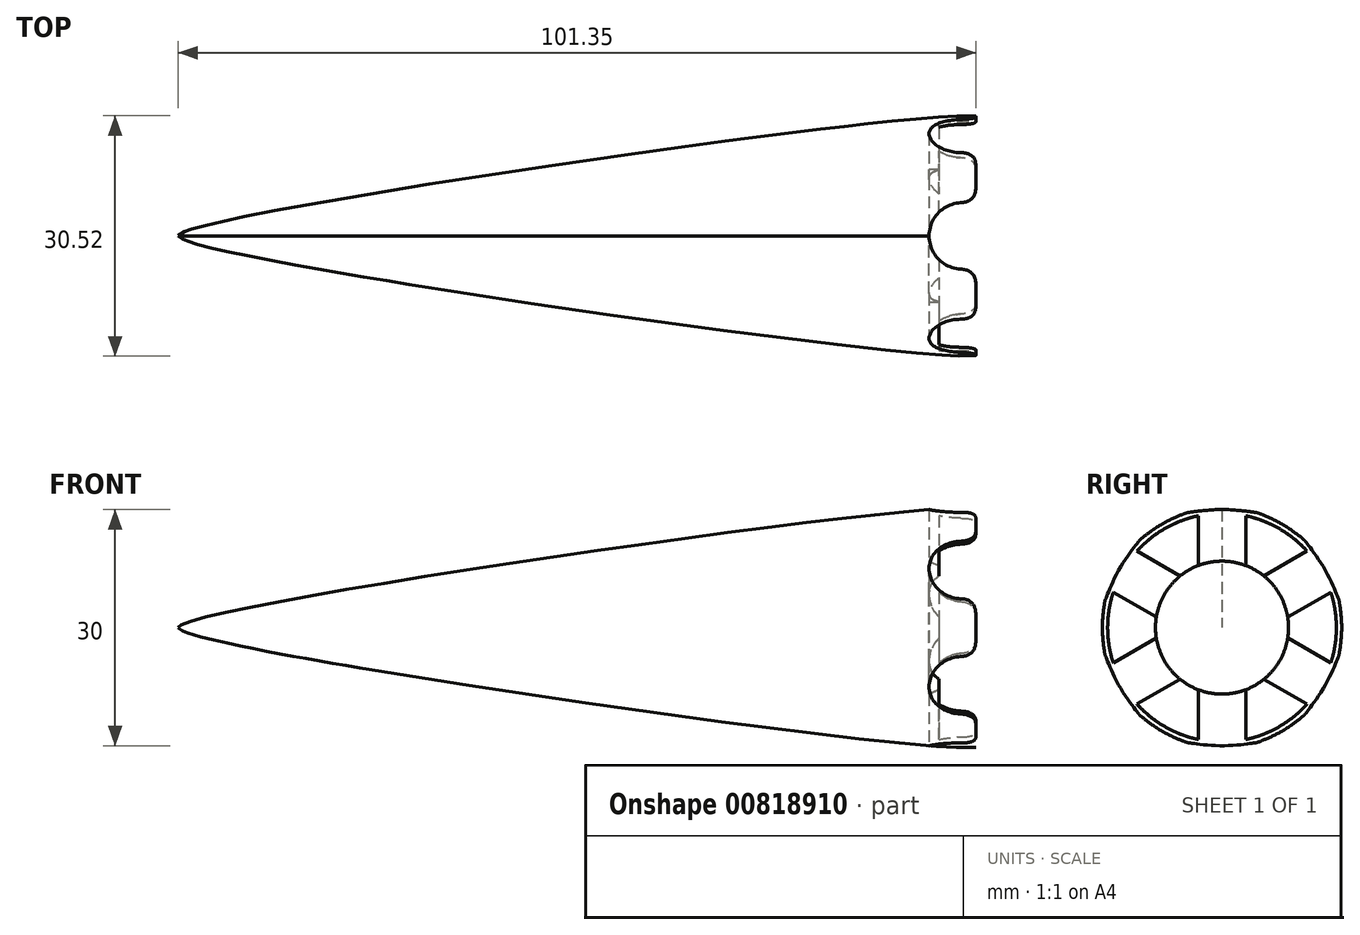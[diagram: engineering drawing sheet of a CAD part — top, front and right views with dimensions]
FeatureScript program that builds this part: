
annotation { "Feature Type Name" : "Feature", "Feature Type Description" : "" }
export const myFeature = defineFeature(function(context is Context, id is Id, definition is map)
    precondition{}
    {
        {
            var Q0;
            Q0=qCreatedBy(makeId("Front.planeOp"),FACE);
            var sketch = newSketch(context, id + "F0", { "sketchPlane" : qUnion([Q0])});
            skFitSpline(sketch, "E0", {"points": [v(1.73, 15.2) * mm, v(-99.62, 0) * mm], "startDerivative": vector(-22.55, 3.1) * mm, "endDerivative": vector(-0.3, -8.2) * mm});
            skLineSegment(sketch, "E1", {"start": v(1.73, 15.2) * mm, "end": v(1.73, 0) * mm});
            skLineSegment(sketch, "E2", {"start": v(1.73, 0) * mm, "end": v(-99.62, 0) * mm});
            skSolve(sketch);
        }
        {
            var Q0;
            Q0=qSketchRegion(id+"F0",true);
            var Q1;
            Q1=sQuery(id+"F0.wireOp",EDGE,"E2");
            revolve(context, id + "F1", {"surfaceOperationType" : NewSurfaceOperationType.NEW, "entities" : qUnion([Q0]), "axis" : qUnion([Q1]), "revolveType" : RevolveType.FULL});
        }
        {
            var Q0;
            Q0=qCreatedBy(makeId("Right.planeOp"),FACE);
            var sketch = newSketch(context, id + "F2", { "sketchPlane" : qUnion([Q0])});
            skCircle(sketch, "E3", {"center": v(0, 0) * mm, "radius": 14.53 * mm});
            skSolve(sketch);
        }
        {
            var Q0;
            Q0=qSketchRegion(id+"F2",true);
            extrude(context, id + "F3", {"entities" : qUnion([Q0]), "operationType" : NewBodyOperationType.REMOVE, "endBound" : BoundingType.SYMMETRIC, "oppositeDirection" : true, "depth" : 5.9 * mm, "offsetDistance" : 25.4 * mm});
        }
        {
            var Q0;
            Q0=qCreatedBy(makeId("Right.planeOp"),FACE);
            var sketch = newSketch(context, id + "F4", { "sketchPlane" : qUnion([Q0])});
            skLineSegment(sketch, "E4.bottom", {"start": v(0, 18.58) * mm, "end": v(-4.22, 18.58) * mm});
            skLineSegment(sketch, "E4.top", {"start": v(0, -18.58) * mm, "end": v(-4.22, -18.58) * mm});
            skLineSegment(sketch, "E4.left", {"start": v(0, 18.58) * mm, "end": v(0, -18.58) * mm});
            skLineSegment(sketch, "E4.right", {"start": v(-4.22, 18.58) * mm, "end": v(-4.22, -18.58) * mm});
            skPoint(sketch, "E4.middle", {"position": v(-2.11, 0) * mm});
            skSolve(sketch);
        }
        {
            var Q0;
            Q0=qCreatedBy(makeId("Right.planeOp"),FACE);
            var sketch = newSketch(context, id + "F5", { "sketchPlane" : qUnion([Q0])});
            skLineSegment(sketch, "E5.bottom", {"start": v(16.1, 9.3) * mm, "end": v(13.98, 12.95) * mm});
            skLineSegment(sketch, "E5.top", {"start": v(-16.1, -9.3) * mm, "end": v(-18.2, -5.63) * mm});
            skLineSegment(sketch, "E5.left", {"start": v(16.1, 9.3) * mm, "end": v(-16.1, -9.3) * mm});
            skLineSegment(sketch, "E5.right", {"start": v(13.98, 12.95) * mm, "end": v(-18.2, -5.63) * mm});
            skPoint(sketch, "E5.middle", {"position": v(-1.06, 1.83) * mm});
            skSolve(sketch);
        }
        {
            var Q0;
            Q0=qCreatedBy(makeId("Right.planeOp"),FACE);
            var sketch = newSketch(context, id + "F6", { "sketchPlane" : qUnion([Q0])});
            skLineSegment(sketch, "E6.bottom", {"start": v(16.1, -9.3) * mm, "end": v(18.2, -5.63) * mm});
            skLineSegment(sketch, "E6.top", {"start": v(-16.1, 9.3) * mm, "end": v(-13.98, 12.95) * mm});
            skLineSegment(sketch, "E6.left", {"start": v(16.1, -9.3) * mm, "end": v(-16.1, 9.3) * mm});
            skLineSegment(sketch, "E6.right", {"start": v(18.2, -5.63) * mm, "end": v(-13.98, 12.95) * mm});
            skPoint(sketch, "E6.middle", {"position": v(1.06, 1.83) * mm});
            skSolve(sketch);
        }
        {
            var Q0;
            Q0=qSketchRegion(id+"F4",true);
            var Q1;
            Q1=sQuery(id+"F4.wireOp",EDGE,"E4.left");
            revolve(context, id + "F7", {"operationType" : NewBodyOperationType.REMOVE, "surfaceOperationType" : NewSurfaceOperationType.NEW, "entities" : qUnion([Q0]), "axis" : qUnion([Q1]), "revolveType" : RevolveType.FULL, "oppositeDirection" : true});
        }
        {
            var Q0;
            Q0=qSketchRegion(id+"F5",true);
            var Q1;
            Q1=sQuery(id+"F5.wireOp",EDGE,"E5.left");
            revolve(context, id + "F8", {"operationType" : NewBodyOperationType.REMOVE, "surfaceOperationType" : NewSurfaceOperationType.NEW, "entities" : qUnion([Q0]), "axis" : qUnion([Q1]), "revolveType" : RevolveType.FULL, "oppositeDirection" : true});
        }
        {
            var Q0;
            Q0=qSketchRegion(id+"F6",true);
            var Q1;
            Q1=sQuery(id+"F6.wireOp",EDGE,"E6.left");
            revolve(context, id + "F9", {"operationType" : NewBodyOperationType.REMOVE, "surfaceOperationType" : NewSurfaceOperationType.NEW, "entities" : qUnion([Q0]), "axis" : qUnion([Q1]), "revolveType" : RevolveType.FULL, "oppositeDirection" : true});
        }
        {
            var Q0;
            Q0=qCreatedBy(makeId("Right.planeOp"),FACE);
            var sketch = newSketch(context, id + "F10", { "sketchPlane" : qUnion([Q0])});
            skCircle(sketch, "E7", {"center": v(0, 0) * mm, "radius": 8.45 * mm});
            skSolve(sketch);
        }
        {
            var Q0;
            Q0=qSketchRegion(id+"F10",true);
            extrude(context, id + "F11", {"entities" : qUnion([Q0]), "operationType" : NewBodyOperationType.REMOVE, "endBound" : BoundingType.SYMMETRIC, "depth" : 8.45 * mm, "offsetDistance" : 25.4 * mm});
        }
        {
            var Q0;
            Q0=makeQuery(id+"F7.boolean.opBoolean","INTERSECT",EDGE,{"disambiguationData":[OD(2.0)],"derivedFrom":[makeQuery(id+"F1.opRevolve","SWEPT_FACE",FACE,{"disambiguationData":[OSD([sQuery(id+"F0.wireOp",EDGE,"E1")])]}),makeQuery(id+"F7.opRevolve","SWEPT_FACE",FACE,{"disambiguationData":[OSD([sQuery(id+"F4.wireOp",EDGE,"E4.right")])]})]});
            var Q1;
            Q1=makeQuery(id+"F9.boolean.opBoolean","INTERSECT",EDGE,{"disambiguationData":[OD(0.0)],"derivedFrom":[makeQuery(id+"F8.boolean.opBoolean","SPLIT",FACE,{"disambiguationData":[OD(1.0)],"derivedFrom":makeQuery(id+"F7.boolean.opBoolean","SPLIT",FACE,{"disambiguationData":[OD(0.0)],"derivedFrom":makeQuery(id+"F1.opRevolve","SWEPT_FACE",FACE,{"disambiguationData":[OSD([sQuery(id+"F0.wireOp",EDGE,"E1")])]})})}),makeQuery(id+"F9.opRevolve","SWEPT_FACE",FACE,{"disambiguationData":[OSD([sQuery(id+"F6.wireOp",EDGE,"E6.right")])]})]});
            var Q2;
            Q2=makeQuery(id+"F9.boolean.opBoolean","INTERSECT",EDGE,{"disambiguationData":[OD(1.0)],"derivedFrom":[makeQuery(id+"F8.boolean.opBoolean","SPLIT",FACE,{"disambiguationData":[OD(1.0)],"derivedFrom":makeQuery(id+"F7.boolean.opBoolean","SPLIT",FACE,{"disambiguationData":[OD(0.0)],"derivedFrom":makeQuery(id+"F1.opRevolve","SWEPT_FACE",FACE,{"disambiguationData":[OSD([sQuery(id+"F0.wireOp",EDGE,"E1")])]})})}),makeQuery(id+"F9.opRevolve","SWEPT_FACE",FACE,{"disambiguationData":[OSD([sQuery(id+"F6.wireOp",EDGE,"E6.right")])]})]});
            var Q3;
            Q3=makeQuery(id+"F8.boolean.opBoolean","INTERSECT",EDGE,{"disambiguationData":[OD(1.0)],"derivedFrom":[makeQuery(id+"F7.boolean.opBoolean","SPLIT",FACE,{"disambiguationData":[OD(0.0)],"derivedFrom":makeQuery(id+"F1.opRevolve","SWEPT_FACE",FACE,{"disambiguationData":[OSD([sQuery(id+"F0.wireOp",EDGE,"E1")])]})}),makeQuery(id+"F8.opRevolve","SWEPT_FACE",FACE,{"disambiguationData":[OSD([sQuery(id+"F5.wireOp",EDGE,"E5.right")])]})]});
            var Q4;
            Q4=makeQuery(id+"F8.boolean.opBoolean","INTERSECT",EDGE,{"disambiguationData":[OD(0.0)],"derivedFrom":[makeQuery(id+"F7.boolean.opBoolean","SPLIT",FACE,{"disambiguationData":[OD(0.0)],"derivedFrom":makeQuery(id+"F1.opRevolve","SWEPT_FACE",FACE,{"disambiguationData":[OSD([sQuery(id+"F0.wireOp",EDGE,"E1")])]})}),makeQuery(id+"F8.opRevolve","SWEPT_FACE",FACE,{"disambiguationData":[OSD([sQuery(id+"F5.wireOp",EDGE,"E5.right")])]})]});
            var Q5;
            Q5=makeQuery(id+"F7.boolean.opBoolean","INTERSECT",EDGE,{"disambiguationData":[OD(0.0)],"derivedFrom":[makeQuery(id+"F1.opRevolve","SWEPT_FACE",FACE,{"disambiguationData":[OSD([sQuery(id+"F0.wireOp",EDGE,"E1")])]}),makeQuery(id+"F7.opRevolve","SWEPT_FACE",FACE,{"disambiguationData":[OSD([sQuery(id+"F4.wireOp",EDGE,"E4.right")])]})]});
            var Q6;
            Q6=makeQuery(id+"F7.boolean.opBoolean","INTERSECT",EDGE,{"disambiguationData":[OD(1.0)],"derivedFrom":[makeQuery(id+"F1.opRevolve","SWEPT_FACE",FACE,{"disambiguationData":[OSD([sQuery(id+"F0.wireOp",EDGE,"E1")])]}),makeQuery(id+"F7.opRevolve","SWEPT_FACE",FACE,{"disambiguationData":[OSD([sQuery(id+"F4.wireOp",EDGE,"E4.right")])]})]});
            var Q7;
            Q7=makeQuery(id+"F9.boolean.opBoolean","INTERSECT",EDGE,{"disambiguationData":[OD(0.0)],"derivedFrom":[makeQuery(id+"F8.boolean.opBoolean","SPLIT",FACE,{"disambiguationData":[OD(0.0)],"derivedFrom":makeQuery(id+"F7.boolean.opBoolean","SPLIT",FACE,{"disambiguationData":[OD(1.0)],"derivedFrom":makeQuery(id+"F1.opRevolve","SWEPT_FACE",FACE,{"disambiguationData":[OSD([sQuery(id+"F0.wireOp",EDGE,"E1")])]})})}),makeQuery(id+"F9.opRevolve","SWEPT_FACE",FACE,{"disambiguationData":[OSD([sQuery(id+"F6.wireOp",EDGE,"E6.right")])]})]});
            var Q8;
            Q8=makeQuery(id+"F9.boolean.opBoolean","INTERSECT",EDGE,{"disambiguationData":[OD(1.0)],"derivedFrom":[makeQuery(id+"F8.boolean.opBoolean","SPLIT",FACE,{"disambiguationData":[OD(0.0)],"derivedFrom":makeQuery(id+"F7.boolean.opBoolean","SPLIT",FACE,{"disambiguationData":[OD(1.0)],"derivedFrom":makeQuery(id+"F1.opRevolve","SWEPT_FACE",FACE,{"disambiguationData":[OSD([sQuery(id+"F0.wireOp",EDGE,"E1")])]})})}),makeQuery(id+"F9.opRevolve","SWEPT_FACE",FACE,{"disambiguationData":[OSD([sQuery(id+"F6.wireOp",EDGE,"E6.right")])]})]});
            var Q9;
            Q9=makeQuery(id+"F8.boolean.opBoolean","INTERSECT",EDGE,{"disambiguationData":[OD(0.0)],"derivedFrom":[makeQuery(id+"F7.boolean.opBoolean","SPLIT",FACE,{"disambiguationData":[OD(1.0)],"derivedFrom":makeQuery(id+"F1.opRevolve","SWEPT_FACE",FACE,{"disambiguationData":[OSD([sQuery(id+"F0.wireOp",EDGE,"E1")])]})}),makeQuery(id+"F8.opRevolve","SWEPT_FACE",FACE,{"disambiguationData":[OSD([sQuery(id+"F5.wireOp",EDGE,"E5.right")])]})]});
            var Q10;
            Q10=makeQuery(id+"F8.boolean.opBoolean","INTERSECT",EDGE,{"disambiguationData":[OD(1.0)],"derivedFrom":[makeQuery(id+"F7.boolean.opBoolean","SPLIT",FACE,{"disambiguationData":[OD(1.0)],"derivedFrom":makeQuery(id+"F1.opRevolve","SWEPT_FACE",FACE,{"disambiguationData":[OSD([sQuery(id+"F0.wireOp",EDGE,"E1")])]})}),makeQuery(id+"F8.opRevolve","SWEPT_FACE",FACE,{"disambiguationData":[OSD([sQuery(id+"F5.wireOp",EDGE,"E5.right")])]})]});
            var Q11;
            Q11=makeQuery(id+"F7.boolean.opBoolean","INTERSECT",EDGE,{"disambiguationData":[OD(3.0)],"derivedFrom":[makeQuery(id+"F1.opRevolve","SWEPT_FACE",FACE,{"disambiguationData":[OSD([sQuery(id+"F0.wireOp",EDGE,"E1")])]}),makeQuery(id+"F7.opRevolve","SWEPT_FACE",FACE,{"disambiguationData":[OSD([sQuery(id+"F4.wireOp",EDGE,"E4.right")])]})]});
            fillet(context, id + "F12", {"entities" : qUnion([Q0, Q1, Q2, Q3, Q4, Q5, Q6, Q7, Q8, Q9, Q10, Q11]), "radius" : 2.03 * mm, "tangentPropagation" : true, "rho" : .5, "crossSection" : FilletCrossSection.CONIC, "allowEdgeOverflow" : false});
        }
    });
